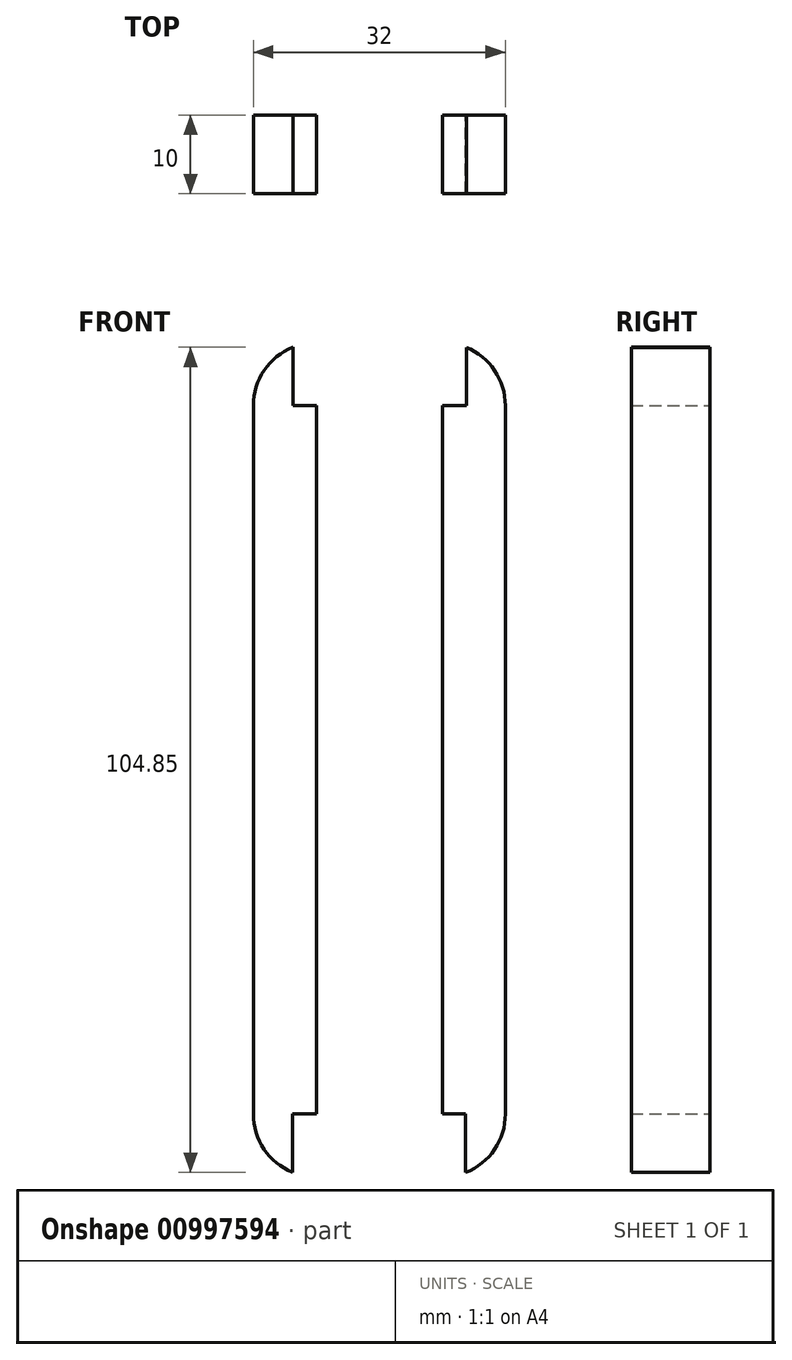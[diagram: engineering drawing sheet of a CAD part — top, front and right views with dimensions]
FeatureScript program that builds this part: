
annotation { "Feature Type Name" : "Feature", "Feature Type Description" : "" }
export const myFeature = defineFeature(function(context is Context, id is Id, definition is map)
    precondition{}
    {
        {
            var Q0;
            Q0=qCreatedBy(makeId("Front.planeOp"),FACE);
            var sketch = newSketch(context, id + "F0", { "sketchPlane" : qUnion([Q0])});
            skLineSegment(sketch, "E0.bottom", {"start": v(8, -45) * mm, "end": v(-8, -45) * mm});
            skLineSegment(sketch, "E0.top", {"start": v(8, 45) * mm, "end": v(-8, 45) * mm});
            skLineSegment(sketch, "E0.left", {"start": v(8, -45) * mm, "end": v(8, 45) * mm});
            skLineSegment(sketch, "E0.right", {"start": v(-8, -45) * mm, "end": v(-8, 45) * mm});
            skPoint(sketch, "E0.middle", {"position": v(0, 0) * mm});
            skLineSegment(sketch, "E1.left", {"start": v(-16, 45) * mm, "end": v(-16, -45) * mm});
            skLineSegment(sketch, "E1.right", {"start": v(16, 45) * mm, "end": v(16, -45) * mm});
            skArc(sketch, "E2", {"start": v(16, 45) * mm, "mid": v(14.64, 49.46) * mm, "end": v(11.03, 52.4) * mm});
            skArc(sketch, "E3", {"start": v(-16, 45) * mm, "mid": v(-14.63, 49.47) * mm, "end": v(-11, 52.42) * mm});
            skPoint(sketch, "E4.orphan", {"position": v(-16, 53) * mm});
            skPoint(sketch, "E5.orphan", {"position": v(16, 53) * mm});
            skArc(sketch, "E6", {"start": v(16, -45) * mm, "mid": v(14.62, -49.49) * mm, "end": v(10.96, -52.43) * mm});
            skArc(sketch, "E7", {"start": v(-16, -45) * mm, "mid": v(-14.65, -49.45) * mm, "end": v(-11.04, -52.4) * mm});
            skPoint(sketch, "E8.orphan", {"position": v(-16, -53) * mm});
            skPoint(sketch, "E9.orphan", {"position": v(16, -53) * mm});
            skLineSegment(sketch, "E10", {"start": v(0, 45) * mm, "end": v(-11, 45) * mm});
            skLineSegment(sketch, "E11", {"start": v(-11, 45) * mm, "end": v(-11, 52.42) * mm});
            skLineSegment(sketch, "E12", {"start": v(0, 45) * mm, "end": v(11.03, 45) * mm});
            skLineSegment(sketch, "E13", {"start": v(11.03, 45) * mm, "end": v(11.03, 52.4) * mm});
            skLineSegment(sketch, "E14", {"start": v(0, -45) * mm, "end": v(-11.04, -45) * mm});
            skLineSegment(sketch, "E15", {"start": v(-11.04, -45) * mm, "end": v(0, -45) * mm});
            skLineSegment(sketch, "E16", {"start": v(0, -45) * mm, "end": v(10.96, -45) * mm});
            skLineSegment(sketch, "E17", {"start": v(10.96, -45) * mm, "end": v(10.96, -52.43) * mm});
            skLineSegment(sketch, "E18", {"start": v(10.96, -52.43) * mm, "end": v(10.96, -45) * mm});
            skLineSegment(sketch, "E19", {"start": v(-11.04, -45) * mm, "end": v(-11.04, -52.43) * mm});
            skLineSegment(sketch, "E20", {"start": v(-11.04, -52.43) * mm, "end": v(-11.06, -52.4) * mm});
            skSolve(sketch);
        }
        {
            var Q0;
            Q0=makeQuery(id+"F0.imprint","IMPRINT",FACE,{"disambiguationData":[TD([[makeQuery(id+"F0.imprint","IMPRINT",EDGE,{"derivedFrom":sQuery(id+"F0.wireOp",EDGE,"E0.right")}),1.0]])]});
            var Q1;
            Q1=makeQuery(id+"F0.imprint","IMPRINT",FACE,{"disambiguationData":[TD([[makeQuery(id+"F0.imprint","IMPRINT",EDGE,{"derivedFrom":sQuery(id+"F0.wireOp",EDGE,"E0.left")}),-1.0]])]});
            extrude(context, id + "F1", {"entities" : qUnion([Q0, Q1]), "endBound" : BoundingType.SYMMETRIC, "depth" : 10 * mm, "offsetDistance" : 25 * mm});
        }
    });
